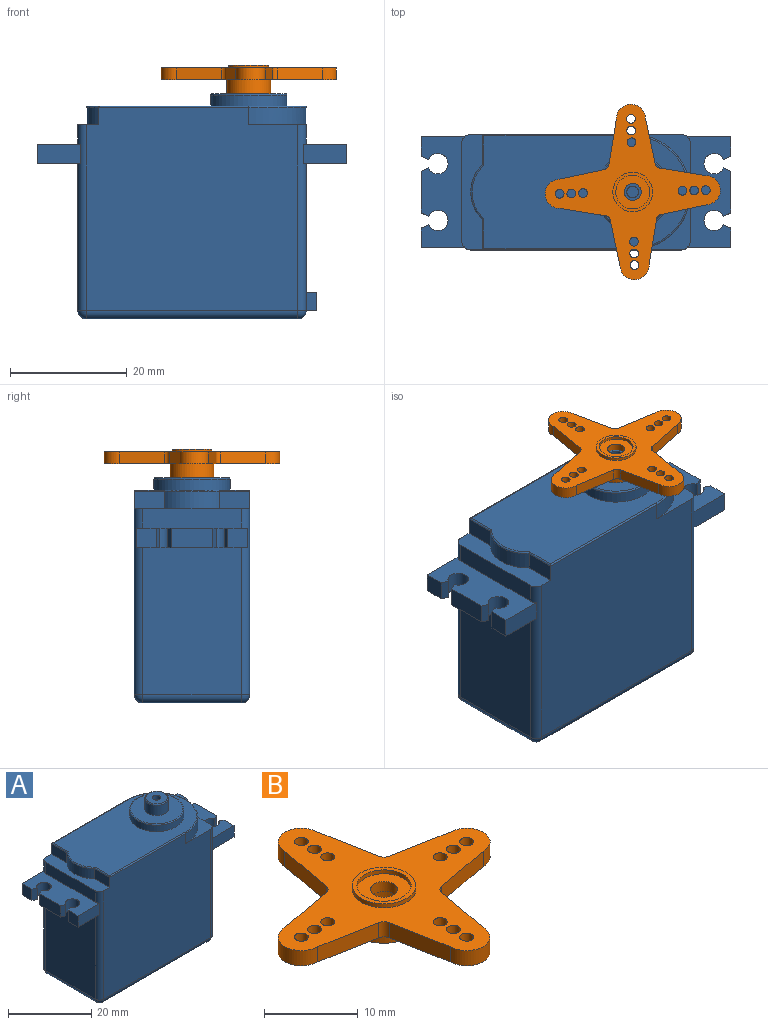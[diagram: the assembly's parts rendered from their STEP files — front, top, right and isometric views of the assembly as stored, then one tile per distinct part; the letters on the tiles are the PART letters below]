
ASSEMBLY  parts=2 mates=1
PART A: 73 faces, bbox 52.9x21.3x41.8 mm
  f0: plane 25.15x16.88mm, normal (1,0,0), area 404.4mm2, adj f20,f46,f47,f48,f58,f59,f61
  f1: plane 16.88x3.3mm, normal (1,0,0), area 55.7mm2, adj f3,f4,f19,f36,f46,f48
  f2: plane 16.88x3.3mm, normal (-1,0,0), area 55.7mm2, adj f5,f25,f51,f54
  f3: plane 9.8x8.86mm, normal (0,0,1), area 19.9mm2, adj f1,f8,f37,f46
  f4: plane 9.8x8.86mm, normal (0,0,1), area 19.9mm2, adj f1,f9,f37,f48
  f5: plane 19.7x3.5mm, normal (0,0,1), area 55.1mm2, adj f2,f8,f9,f38,f39,f40,f51,f54
  f6: plane 25.15x16.88mm, normal (-1,0,0), area 424.5mm2, adj f26,f51,f54,f57
  f7: plane 36.18x16.88mm, normal (0,0,-1), area 610.7mm2, adj f47,f52,f53,f57
  f8: plane 36.18x34.74mm, normal (0,-1,0), area 1226mm2, adj f3,f5,f37,f40,f46,f51,f52,f66
  f9: plane 36.18x34.74mm, normal (0,1,0), area 1226mm2, adj f4,f5,f37,f38,f48,f53,f54,f67
  f10: plane 3.38x3.34mm, normal (1,0,0), area 11.3mm2, adj f11,f19,f20,f22
  f11: plane 3.34x1.21mm, normal (0.41,0.91,0), area 4.4mm2, adj f10,f12,f19,f20
  f12: cylinder r=1.75mm len=3.5mm, axis (0,0,-1), area 31.8mm2, adj f11,f13,f19,f20
  f13: plane 3.34x1.21mm, normal (0.41,-0.91,0), area 4.4mm2, adj f12,f14,f19,f20
  f14: plane 7.16x3.34mm, normal (1,0,0), area 23.9mm2, adj f13,f15,f19,f20
  f15: plane 3.34x1.21mm, normal (0.41,0.91,0), area 4.4mm2, adj f14,f16,f19,f20
  f16: cylinder r=1.75mm len=3.5mm, axis (0,0,-1), area 31.8mm2, adj f15,f17,f19,f20
  f17: plane 3.34x1.21mm, normal (0.41,-0.91,0), area 4.4mm2, adj f16,f18,f19,f20
  f18: plane 3.38x3.34mm, normal (1,0,0), area 11.3mm2, adj f17,f19,f20,f21
  f19: plane 19x7.41mm, normal (0,0,1), area 108.2mm2, adj f1,f10,f11,f12,f13,f14,f15,f16
  f20: plane 19x7.41mm, normal (0,0,-1), area 108.2mm2, adj f0,f10,f11,f12,f13,f14,f15,f16
  f21: plane 7.41x3.34mm, normal (0,1,0), area 24.8mm2, adj f18,f19,f20,f48
  f22: plane 7.41x3.34mm, normal (0,-1,0), area 24.8mm2, adj f10,f19,f20,f46
  f23: plane 7.41x3.34mm, normal (0,-1,0), area 24.8mm2, adj f25,f26,f29,f51
  f24: plane 7.41x3.34mm, normal (0,1,0), area 24.8mm2, adj f25,f26,f30,f54
  f25: plane 19x7.41mm, normal (0,0,1), area 108.2mm2, adj f2,f23,f24,f27,f28,f29,f30,f31
  f26: plane 19x7.41mm, normal (0,0,-1), area 108.2mm2, adj f6,f23,f24,f27,f28,f29,f30,f31
  f27: cylinder r=1.75mm len=3.5mm, axis (0,0,-1), area 31.8mm2, adj f25,f26,f28,f35
  f28: plane 3.34x1.21mm, normal (-0.41,0.91,0), area 4.4mm2, adj f25,f26,f27,f29
  f29: plane 3.38x3.34mm, normal (-1,0,0), area 11.3mm2, adj f23,f25,f26,f28
  f30: plane 3.38x3.34mm, normal (-1,0,0), area 11.3mm2, adj f24,f25,f26,f31
  f31: plane 3.34x1.21mm, normal (-0.41,-0.91,0), area 4.4mm2, adj f25,f26,f30,f32
  f32: cylinder r=1.75mm len=3.5mm, axis (0,0,-1), area 31.8mm2, adj f25,f26,f31,f33
  f33: plane 3.34x1.21mm, normal (-0.41,0.91,0), area 4.4mm2, adj f25,f26,f32,f34
  f34: plane 7.16x3.34mm, normal (-1,0,0), area 23.9mm2, adj f25,f26,f33,f35
  f35: plane 3.34x1.21mm, normal (-0.41,-0.91,0), area 4.4mm2, adj f25,f26,f27,f34
  f36: plane 1.98x0.05mm, normal (0,0,-1), area 0.1mm2, adj f1,f37
  f37: cylinder r=9.85mm len=19.7mm, axis (0,0,-1), area 91.3mm2, adj f3,f4,f8,f9,f36,f65
  f38: plane 5.16x2.95mm, normal (-1,0,0), area 15.2mm2, adj f5,f9,f39,f69
  f39: cylinder r=6.5mm len=9.38mm, axis (0,0,-1), area 30.9mm2, adj f5,f38,f40,f70
  f40: plane 5.16x2.95mm, normal (-1,0,0), area 15.2mm2, adj f5,f8,f39,f68
  f41: plane 37.05x19.2mm, normal (0,0,1), area 513.3mm2, adj f42,f65,f66,f67,f68,f69,f70
  f42: cylinder r=6.5mm len=13mm, axis (0,0,-1), area 76.4mm2, adj f41,f71
  f43: plane 12.5x12.5mm, normal (0,0,1), area 97.6mm2, adj f44,f71
  f44: cylinder r=2.82mm len=5.65mm, axis (0,0,-1), area 53.2mm2, adj f43,f72
  f45: plane 5.15x5.15mm, normal (0,0,1), area 17.7mm2, adj f63,f72
  f46: cylinder r=1.41mm len=31.79mm, axis (0,0,-1), area 66.4mm2, adj f0,f1,f3,f8,f19,f20,f22,f49
  f47: cylinder r=1.41mm len=16.88mm, axis (0,-1,0), area 37.4mm2, adj f0,f7,f49,f50,f60
  f48: cylinder r=1.41mm len=31.79mm, axis (0,0,1), area 66.4mm2, adj f0,f1,f4,f9,f19,f20,f21,f50
  f49: sphere r=1.41mm, area 3.1mm2, adj f46,f47,f52
  f50: sphere r=1.41mm, area 3.1mm2, adj f47,f48,f53
  f51: cylinder r=1.41mm len=31.79mm, axis (0,0,1), area 66.4mm2, adj f2,f5,f6,f8,f23,f25,f26,f55
  f52: cylinder r=1.41mm len=36.18mm, axis (-1,0,0), area 80.1mm2, adj f7,f8,f49,f55
  f53: cylinder r=1.41mm len=36.18mm, axis (1,0,0), area 80.1mm2, adj f7,f9,f50,f56
  f54: cylinder r=1.41mm len=31.79mm, axis (0,0,-1), area 66.4mm2, adj f2,f5,f6,f9,f24,f25,f26,f56
  f55: sphere r=1.41mm, area 3.1mm2, adj f51,f52,f57
  f56: sphere r=1.41mm, area 3.1mm2, adj f53,f54,f57
  f57: cylinder r=1.41mm len=16.88mm, axis (0,1,0), area 37.4mm2, adj f6,f7,f55,f56
  f58: plane 6.4x1.75mm, normal (0,0,1), area 11.2mm2, adj f0,f59,f61,f62
  f59: plane 3.15x1.75mm, normal (0,-1,0), area 5.5mm2, adj f0,f58,f60,f62
  f60: plane 6.4x1.75mm, normal (0,0,-1), area 11.2mm2, adj f47,f59,f61,f62
  f61: plane 3.15x1.75mm, normal (0,1,0), area 5.5mm2, adj f0,f58,f60,f62
  f62: plane 6.4x3.15mm, normal (1,0,0), area 20.2mm2, adj f58,f59,f60,f61
  f63: cylinder r=1mm len=6mm, axis (0,0,1), area 37.7mm2, adj f45,f64
  f64: plane 2x2mm, normal (0,0,1), area 3.1mm2, adj f63
  f65: torus R=9.6mm, axis (0,0,1), area 12mm2, adj f37,f41,f66,f67
  f66: cylinder r=0.25mm len=25.7mm, axis (1,0,0), area 10.1mm2, adj f8,f41,f65,f68
  f67: cylinder r=0.25mm len=25.7mm, axis (-1,0,0), area 10.1mm2, adj f9,f41,f65,f69
  f68: cylinder r=0.25mm len=5.27mm, axis (0,1,0), area 2mm2, adj f40,f41,f66,f70
  f69: cylinder r=0.25mm len=5.27mm, axis (0,1,0), area 2mm2, adj f38,f41,f67,f70
  f70: torus R=6.25mm, axis (0,0,1), area 4.1mm2, adj f39,f41,f68,f69
  f71: torus R=6.25mm, axis (0,0,1), area 15.8mm2, adj f42,f43
  f72: torus R=2.58mm, axis (0,0,1), area 6.7mm2, adj f44,f45
PART B: 39 faces, bbox 30x30x4.9 mm
  f0: plane 7.75x2mm, normal (0.18,0.98,0), area 15.8mm2, adj f1,f27,f28,f29
  f1: cylinder r=1mm len=2mm, axis (0,0,-1), area 2.4mm2, adj f0,f2,f28,f29
  f2: plane 7.75x2mm, normal (0.98,0.18,0), area 15.8mm2, adj f1,f3,f28,f29
  f3: cylinder r=2.5mm len=5mm, axis (0,0,-1), area 15.7mm2, adj f2,f4,f28,f29
  f4: plane 7.75x2mm, normal (-0.98,0.18,0), area 15.8mm2, adj f3,f5,f28,f29
  f5: cylinder r=1mm len=2mm, axis (0,0,-1), area 2.4mm2, adj f4,f6,f28,f29
  f6: plane 7.75x2mm, normal (-0.18,0.98,0), area 15.8mm2, adj f5,f7,f28,f29
  f7: cylinder r=2.5mm len=5mm, axis (0,0,-1), area 15.7mm2, adj f6,f8,f28,f29
  f8: plane 7.75x2mm, normal (-0.18,-0.98,0), area 15.8mm2, adj f7,f9,f28,f29
  f9: cylinder r=1mm len=2mm, axis (0,0,-1), area 2.4mm2, adj f8,f10,f28,f29
  f10: plane 7.75x2mm, normal (-0.98,-0.18,0), area 15.8mm2, adj f9,f11,f28,f29
  f11: cylinder r=2.5mm len=5mm, axis (0,0,-1), area 15.7mm2, adj f10,f12,f28,f29
  f12: plane 7.75x2mm, normal (0.98,-0.18,0), area 15.8mm2, adj f11,f13,f28,f29
  f13: cylinder r=1mm len=2mm, axis (0,0,-1), area 2.4mm2, adj f12,f14,f28,f29
  f14: plane 7.75x2mm, normal (0.18,-0.98,0), area 15.8mm2, adj f13,f27,f28,f29
  f15: cylinder r=0.75mm len=2mm, axis (0,0,-1), area 9.4mm2, adj f28,f29
  f16: cylinder r=0.75mm len=2mm, axis (0,0,-1), area 9.4mm2, adj f28,f29
  f17: cylinder r=0.75mm len=2mm, axis (0,0,-1), area 9.4mm2, adj f28,f29
  f18: cylinder r=0.75mm len=2mm, axis (0,0,-1), area 9.4mm2, adj f28,f29
  f19: cylinder r=0.75mm len=2mm, axis (0,0,-1), area 9.4mm2, adj f28,f29
  f20: cylinder r=0.75mm len=2mm, axis (0,0,-1), area 9.4mm2, adj f28,f29
  f21: cylinder r=0.75mm len=2mm, axis (0,0,-1), area 9.4mm2, adj f28,f29
  f22: cylinder r=0.75mm len=2mm, axis (0,0,-1), area 9.4mm2, adj f28,f29
  f23: cylinder r=0.75mm len=2mm, axis (0,0,-1), area 9.4mm2, adj f28,f29
  f24: cylinder r=0.75mm len=2mm, axis (0,0,-1), area 9.4mm2, adj f28,f29
  f25: cylinder r=0.75mm len=2mm, axis (0,0,-1), area 9.4mm2, adj f28,f29
  f26: cylinder r=0.75mm len=2mm, axis (0,0,-1), area 9.4mm2, adj f28,f29
  f27: cylinder r=2.5mm len=5mm, axis (0,0,-1), area 15.7mm2, adj f0,f14,f28,f29
  f28: plane 30x30mm, normal (0,0,1), area 270.4mm2, adj f0,f1,f2,f3,f4,f5,f6,f7
  f29: plane 30x30mm, normal (0,0,-1), area 262.3mm2, adj f0,f1,f2,f3,f4,f5,f6,f7
  f30: cylinder r=2.9mm len=5.8mm, axis (0,0,-1), area 9.1mm2, adj f32,f33
  f31: cylinder r=3.4mm len=6.8mm, axis (0,0,-1), area 10.7mm2, adj f28,f32
  f32: plane 6.8x6.8mm, normal (0,0,1), area 9.9mm2, adj f30,f31
  f33: plane 5.8x5.8mm, normal (0,0,1), area 19.8mm2, adj f30,f38
  f34: cylinder r=3.76mm len=7.52mm, axis (0,0,1), area 56.7mm2, adj f29,f35
  f35: plane 7.52x7.52mm, normal (0,0,-1), area 17.1mm2, adj f34,f36
  f36: cylinder r=2.95mm len=5.9mm, axis (0,0,-1), area 57.5mm2, adj f35,f37
  f37: plane 5.9x5.9mm, normal (0,0,-1), area 20.7mm2, adj f36,f38
  f38: cylinder r=1.45mm len=2.9mm, axis (0,0,-1), area 11.8mm2, adj f33,f37
PLACE A t=(-8.4,-3.39,2.14)mm fixed
PLACE B rot(axis=(0,0,-1),178.6deg) t=(-8.4,-3.39,16.5)mm
MATE revolute B.f36 <-> A.f44  axis (0,0,-1) through (-8.4,-3.39,14.1)mm
